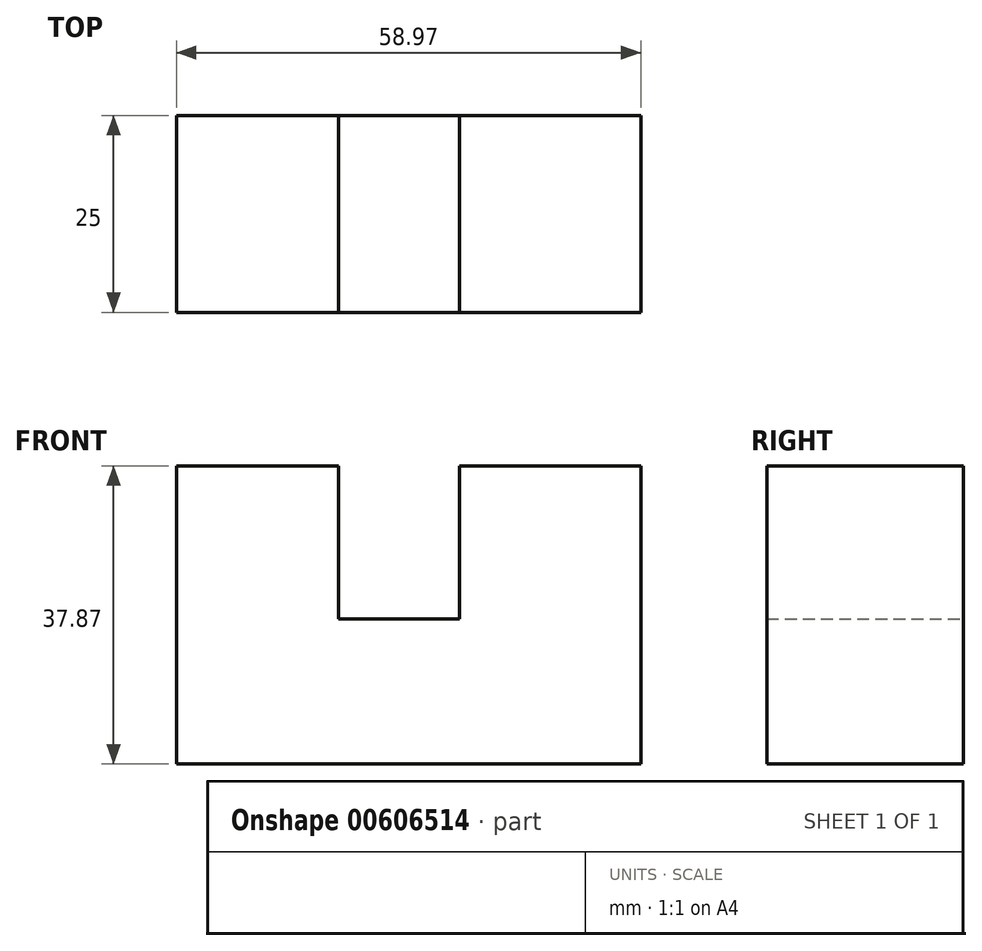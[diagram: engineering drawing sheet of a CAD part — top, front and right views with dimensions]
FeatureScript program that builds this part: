
annotation { "Feature Type Name" : "Feature", "Feature Type Description" : "" }
export const myFeature = defineFeature(function(context is Context, id is Id, definition is map)
    precondition{}
    {
        {
            var Q0;
            Q0=qCreatedBy(makeId("Front.planeOp"),FACE);
            var sketch = newSketch(context, id + "F0", { "sketchPlane" : qUnion([Q0])});
            skLineSegment(sketch, "E0", {"start": v(-56.52, -32.36) * mm, "end": v(2.45, -32.36) * mm});
            skLineSegment(sketch, "E1", {"start": v(2.45, -13.92) * mm, "end": v(-56.27, -13.92) * mm});
            skLineSegment(sketch, "E2", {"start": v(2.45, -13.92) * mm, "end": v(2.45, -32.36) * mm});
            skLineSegment(sketch, "E3", {"start": v(-56.52, -32.36) * mm, "end": v(-56.52, 5.51) * mm});
            skLineSegment(sketch, "E4", {"start": v(-56.52, 5.51) * mm, "end": v(-35.93, 5.51) * mm});
            skLineSegment(sketch, "E5", {"start": v(-35.93, 5.51) * mm, "end": v(-35.93, -32.36) * mm});
            skLineSegment(sketch, "E6", {"start": v(2.45, -32.36) * mm, "end": v(2.45, 5.51) * mm});
            skLineSegment(sketch, "E7", {"start": v(2.45, 5.51) * mm, "end": v(-20.58, 5.51) * mm});
            skLineSegment(sketch, "E8", {"start": v(-20.58, 5.51) * mm, "end": v(-20.58, -32.36) * mm});
            skLineSegment(sketch, "E9", {"start": v(-56.52, -13.92) * mm, "end": v(-56.52, -32.36) * mm});
            skSolve(sketch);
        }
        {
            var Q0;
            Q0 = qSketchRegion(id + "F0", true);
            extrude(context, id + "F1", {"entities" : qUnion([Q0]), "depth" : 25 * mm, "offsetDistance" : 25 * mm});
        }
    });
